FCSTD DOCUMENT  (FreeCAD 0.18R16131 (Git))
Label: plate_cutouts
License: All rights reserved
LicenseURL: http://en.wikipedia.org/wiki/All_rights_reserved
objects: Sketcher::SketchObject×6, Spreadsheet::Sheet×1
note: 6 computed .brp shape members not serialized (recipe doc carries the construction recipe); baked Part::Feature solids carry a one-line shape summary decoded from their .brp

FEATURE [Sketcher::SketchObject] Sketch  label="alps"
  expr: Constraints[10] = dimensions.alps_h + dimensions.oversize
  expr: Constraints[9] = dimensions.alps_w + dimensions.oversize
  sketch-geometry (4):
    g0: LineSegment StartX=-7.8 StartY=-6.4 StartZ=0 EndX=7.8 EndY=-6.4 EndZ=0
    g1: LineSegment StartX=7.8 StartY=-6.4 StartZ=0 EndX=7.8 EndY=6.4 EndZ=0
    g2: LineSegment StartX=7.8 StartY=6.4 StartZ=0 EndX=-7.8 EndY=6.4 EndZ=0
    g3: LineSegment StartX=-7.8 StartY=6.4 StartZ=0 EndX=-7.8 EndY=-6.4 EndZ=0
  constraints (11):
    c: Coincident(g0,g1)
    c: Coincident(g1,g2)
    c: Coincident(g2,g3)
    c: Coincident(g3,g0)
    c: Horizontal(g0)
    c: Horizontal(g2)
    c: Vertical(g1)
    c: Vertical(g3)
    c: Symmetric(g1,g0,g-1)
    c: Distance(g2) = 15.6
    c: Distance(g1) = 12.8
FEATURE [Sketcher::SketchObject] Sketch001  label="mx"
  MapMode = 5
  expr: Constraints[10] = dimensions.mx_h + dimensions.oversize
  expr: Constraints[9] = dimensions.mx_w + dimensions.oversize
  sketch-geometry (4):
    g0: LineSegment StartX=-7 StartY=-7 StartZ=0 EndX=7 EndY=-7 EndZ=0
    g1: LineSegment StartX=7 StartY=-7 StartZ=0 EndX=7 EndY=7 EndZ=0
    g2: LineSegment StartX=7 StartY=7 StartZ=0 EndX=-7 EndY=7 EndZ=0
    g3: LineSegment StartX=-7 StartY=7 StartZ=0 EndX=-7 EndY=-7 EndZ=0
  constraints (11):
    c: Coincident(g0,g1)
    c: Coincident(g1,g2)
    c: Coincident(g2,g3)
    c: Coincident(g3,g0)
    c: Horizontal(g0)
    c: Horizontal(g2)
    c: Vertical(g1)
    c: Vertical(g3)
    c: Symmetric(g1,g0,g-1)
    c: Distance(g2) = 14
    c: Distance(g1) = 14
FEATURE [Spreadsheet::Sheet] Spreadsheet  label="dimensions"
  cells = A2=mx height; B2(mx_h)=14; A3=mx width; B3(mx_w)=14; A5=alps height; B5(alps_h)=12.8; A6=alps width; B6(alps_w)=15.6; C6=nominal + 0.10; A8=corner radius; B8(in_rad)=0.5; A9=over/under size; B9(oversize)=0; A10=corner relief angle; B10(corner_angle)=45; A12=alps stab CU height; B12(alps_stab_cu_height)=5; A13=alps stab CU width; B13(alps_stab_cu_width)=2.5; A14=alps stab height pos; B14(alps_stab_pos_height)=9.1; A15=alps stab width pos; B15(alps_stab_pos_width)==31 / 2; A17=mx stab pos height; B17(mx_stab_pos_h)=6.77; A18=mx stab pos width; B18(mx_stab_pos_w)=15.33; C18=nominal + 0.05; A19=mx stab main height; B19(mx_stab_main_h)=12.4; C19=nominal + 0.10; A20=mx stab main width; B20(mx_stab_main_w)=6.85; C20=nominal + 0.10; A21=mx stab vert height; B21(mx_stab_vert_h)=13.5; A22=mx stab vert width; B22(mx_stab_vert_w)=3.3; A23=mx stab hor height; B23(mx_stab_hor_h)=2.8; A24=mx stab hor width; B24(mx_stab_hor_w)=7.65; C24=nominal + 0.10; A25=mx stab hor pos; B25(mx_stab_hor_pos)=6.27
FEATURE [Sketcher::SketchObject] Sketch002  label="mx_rounded"
  ExternalGeometry = -> [Sketch001]
  expr: Constraints[5] = dimensions.in_rad
  expr: Constraints[4] = dimensions.corner_angle
  sketch-geometry (12):
    g0: LineSegment [constr] StartX=-7 StartY=7 StartZ=0 EndX=-6.64645 EndY=6.64645 EndZ=0
    g1: LineSegment [constr] StartX=7 StartY=7 StartZ=0 EndX=6.64645 EndY=6.64645 EndZ=0
    g2: LineSegment [constr] StartX=7 StartY=-7 StartZ=0 EndX=6.64645 EndY=-6.64645 EndZ=0
    g3: LineSegment [constr] StartX=-7 StartY=-7 StartZ=0 EndX=-6.64645 EndY=-6.64645 EndZ=0
    g4: ArcOfCircle CenterX=-6.64645 CenterY=6.64645 CenterZ=0 NormalX=0 NormalY=0 NormalZ=1 AngleXU=0 Radius=0.5 StartAngle=0.785398 EndAngle=3.92699
    g5: ArcOfCircle CenterX=6.64645 CenterY=6.64645 CenterZ=0 NormalX=0 NormalY=0 NormalZ=1 AngleXU=0 Radius=0.5 StartAngle=5.49779 EndAngle=8.63938
    g6: ArcOfCircle CenterX=6.64645 CenterY=-6.64645 CenterZ=0 NormalX=0 NormalY=0 NormalZ=1 AngleXU=0 Radius=0.5 StartAngle=3.92699 EndAngle=7.06858
    g7: ArcOfCircle CenterX=-6.64645 CenterY=-6.64645 CenterZ=0 NormalX=0 NormalY=0 NormalZ=1 AngleXU=0 Radius=0.5 StartAngle=2.35619 EndAngle=5.49779
    g8: LineSegment StartX=-6.29289 StartY=7 StartZ=0 EndX=6.29289 EndY=7 EndZ=0
    g9: LineSegment StartX=-7 StartY=-6.29289 StartZ=0 EndX=-7 EndY=6.29289 EndZ=0
    g10: LineSegment StartX=7 StartY=6.29289 StartZ=0 EndX=7 EndY=-6.29289 EndZ=0
    g11: LineSegment StartX=6.29289 StartY=-7 StartZ=0 EndX=-6.29289 EndY=-7 EndZ=0
  constraints (33):
    c: Coincident(g0,g-4)
    c: Coincident(g1,g-6)
    c: Coincident(g2,g-6)
    c: Coincident(g3,g-5)
    c: Angle(g-4,g0) = 0.785398
    c: Distance(g0) = 0.5
    c: Symmetric(g1,g0,g-2)
    c: Symmetric(g0,g3,g-1)
    c: Symmetric(g3,g2,g-2)
    c: PointOnObject(g4,g-3)
    c: PointOnObject(g4,g-4)
    c: PointOnObject(g0,g4)
    c: Coincident(g4,g0)
    c: PointOnObject(g5,g-3)
    c: PointOnObject(g5,g-6)
    c: PointOnObject(g1,g5)
    c: Coincident(g5,g1)
    c: PointOnObject(g6,g-6)
    c: PointOnObject(g6,g-5)
    c: PointOnObject(g2,g6)
    c: Coincident(g6,g2)
    c: PointOnObject(g7,g-4)
    c: PointOnObject(g7,g-5)
    c: PointOnObject(g3,g7)
    c: Coincident(g7,g3)
    c: Coincident(g8,g4)
    c: Coincident(g9,g7)
    c: Coincident(g10,g5)
    c: Coincident(g11,g6)
    c: Coincident(g8,g5)
    c: Coincident(g10,g6)
    c: Coincident(g11,g7)
    c: Coincident(g9,g4)
FEATURE [Sketcher::SketchObject] Sketch003  label="alps_rounded"
  ExternalGeometry = -> [Sketch]
  MapMode = 2
  Support = -> [Sketch002]
  expr: Constraints[8] = dimensions.corner_angle
  expr: Constraints[3] = dimensions.in_rad
  sketch-geometry (12):
    g0: LineSegment [constr] StartX=-7.8 StartY=6.4 StartZ=0 EndX=-7.44645 EndY=6.04645 EndZ=0
    g1: LineSegment [constr] StartX=7.8 StartY=6.4 StartZ=0 EndX=7.44645 EndY=6.04645 EndZ=0
    g2: LineSegment [constr] StartX=7.8 StartY=-6.4 StartZ=0 EndX=7.44645 EndY=-6.04645 EndZ=0
    g3: LineSegment [constr] StartX=-7.8 StartY=-6.4 StartZ=0 EndX=-7.44645 EndY=-6.04645 EndZ=0
    g4: ArcOfCircle CenterX=-7.44645 CenterY=6.04645 CenterZ=0 NormalX=0 NormalY=0 NormalZ=1 AngleXU=0 Radius=0.5 StartAngle=0.785398 EndAngle=3.92699
    g5: ArcOfCircle CenterX=7.44645 CenterY=6.04645 CenterZ=0 NormalX=0 NormalY=0 NormalZ=1 AngleXU=0 Radius=0.5 StartAngle=5.49779 EndAngle=8.63938
    g6: ArcOfCircle CenterX=7.44645 CenterY=-6.04645 CenterZ=0 NormalX=0 NormalY=0 NormalZ=1 AngleXU=0 Radius=0.5 StartAngle=3.92699 EndAngle=7.06858
    g7: ArcOfCircle CenterX=-7.44645 CenterY=-6.04645 CenterZ=0 NormalX=0 NormalY=0 NormalZ=1 AngleXU=0 Radius=0.5 StartAngle=2.35619 EndAngle=5.49779
    g8: LineSegment StartX=-7.8 StartY=-5.69289 StartZ=0 EndX=-7.8 EndY=5.69289 EndZ=0
    g9: LineSegment StartX=-7.09289 StartY=6.4 StartZ=0 EndX=7.09289 EndY=6.4 EndZ=0
    g10: LineSegment StartX=7.8 StartY=5.69289 StartZ=0 EndX=7.8 EndY=-5.69289 EndZ=0
    g11: LineSegment StartX=7.09289 StartY=-6.4 StartZ=0 EndX=-7.09289 EndY=-6.4 EndZ=0
  constraints (33):
    c: Coincident(g1,g-6)
    c: Coincident(g2,g-6)
    c: Coincident(g3,g-5)
    c: Distance(g0) = 0.5
    c: Coincident(g0,g-4)
    c: Symmetric(g0,g1,g-2)
    c: Symmetric(g0,g3,g-1)
    c: Symmetric(g3,g2,g-2)
    c: Angle(g-4,g0) = 0.785398
    c: PointOnObject(g4,g-3)
    c: PointOnObject(g4,g-4)
    c: PointOnObject(g0,g4)
    c: Coincident(g4,g0)
    c: PointOnObject(g5,g-3)
    c: PointOnObject(g5,g-6)
    c: PointOnObject(g1,g5)
    c: Coincident(g5,g1)
    c: PointOnObject(g6,g-6)
    c: PointOnObject(g6,g-5)
    c: PointOnObject(g2,g6)
    c: Coincident(g6,g2)
    c: PointOnObject(g7,g-4)
    c: PointOnObject(g7,g-5)
    c: PointOnObject(g3,g7)
    c: Coincident(g7,g3)
    c: Coincident(g8,g7)
    c: Coincident(g9,g4)
    c: Coincident(g10,g5)
    c: Coincident(g11,g6)
    c: Coincident(g11,g7)
    c: Coincident(g8,g4)
    c: Coincident(g9,g5)
    c: Coincident(g10,g6)
FEATURE [Sketcher::SketchObject] Sketch004  label="mx_2u_stab"
  ExternalGeometry = -> [Sketch001]
  MapMode = 2
  Support = -> [Sketch003]
  expr: Constraints[36] = dimensions.mx_stab_pos_w
  expr: Constraints[34] = dimensions.mx_stab_hor_w + dimensions.oversize
  expr: Constraints[35] = dimensions.mx_stab_pos_h
  expr: Constraints[85] = dimensions.mx_stab_hor_pos
  expr: Constraints[33] = dimensions.mx_stab_vert_h + dimensions.oversize
  expr: Constraints[31] = dimensions.mx_stab_main_h + dimensions.oversize
  expr: Constraints[30] = dimensions.mx_stab_vert_w + dimensions.oversize
  expr: Constraints[32] = dimensions.mx_stab_hor_h + dimensions.oversize
  expr: Constraints[29] = dimensions.mx_stab_main_w + dimensions.oversize
  sketch-geometry (49):
    g0: LineSegment [constr] StartX=-8.48 StartY=5.63 StartZ=0 EndX=-8.48 EndY=-6.77 EndZ=0
    g1: LineSegment [constr] StartX=-8.48 StartY=-6.77 StartZ=0 EndX=-15.33 EndY=-6.77 EndZ=0
    g2: LineSegment [constr] StartX=-15.33 StartY=-6.77 StartZ=0 EndX=-15.33 EndY=5.63 EndZ=0
    g3: LineSegment [constr] StartX=-16.13 StartY=2.3 StartZ=0 EndX=-8.48 EndY=2.3 EndZ=0
    g4: LineSegment [constr] StartX=-8.48 StartY=2.3 StartZ=0 EndX=-8.48 EndY=-0.5 EndZ=0
    g5: LineSegment [constr] StartX=-8.48 StartY=-0.5 StartZ=0 EndX=-16.13 EndY=-0.5 EndZ=0
    g6: LineSegment [constr] StartX=-16.13 StartY=-0.5 StartZ=0 EndX=-16.13 EndY=2.3 EndZ=0
    g7: LineSegment [constr] StartX=-13.555 StartY=5.63 StartZ=0 EndX=-10.255 EndY=5.63 EndZ=0
    g8: LineSegment [constr] StartX=-10.255 StartY=5.63 StartZ=0 EndX=-10.255 EndY=-7.87 EndZ=0
    g9: LineSegment [constr] StartX=-10.255 StartY=-7.87 StartZ=0 EndX=-13.555 EndY=-7.87 EndZ=0
    g10: LineSegment [constr] StartX=-13.555 StartY=-7.87 StartZ=0 EndX=-13.555 EndY=5.63 EndZ=0
    g11: LineSegment [constr] StartX=-15.33 StartY=5.63 StartZ=0 EndX=-13.555 EndY=5.63 EndZ=0
    g12: LineSegment [constr] StartX=-10.255 StartY=5.63 StartZ=0 EndX=-8.48 EndY=5.63 EndZ=0
    g13: LineSegment StartX=-8.48 StartY=5.63 StartZ=0 EndX=-15.33 EndY=5.63 EndZ=0
    g14: LineSegment StartX=-15.33 StartY=5.63 StartZ=0 EndX=-15.33 EndY=2.3 EndZ=0
    g15: LineSegment StartX=-15.33 StartY=2.3 StartZ=0 EndX=-16.13 EndY=2.3 EndZ=0
    g16: LineSegment StartX=-16.13 StartY=2.3 StartZ=0 EndX=-16.13 EndY=-0.5 EndZ=0
    g17: LineSegment StartX=-16.13 StartY=-0.5 StartZ=0 EndX=-15.33 EndY=-0.5 EndZ=0
    g18: LineSegment StartX=-15.33 StartY=-0.5 StartZ=0 EndX=-15.33 EndY=-6.77 EndZ=0
    g19: LineSegment StartX=-15.33 StartY=-6.77 StartZ=0 EndX=-13.555 EndY=-6.77 EndZ=0
    g20: LineSegment StartX=-13.555 StartY=-6.77 StartZ=0 EndX=-13.555 EndY=-7.87 EndZ=0
    g21: LineSegment StartX=-13.555 StartY=-7.87 StartZ=0 EndX=-10.255 EndY=-7.87 EndZ=0
    g22: LineSegment StartX=-10.255 StartY=-7.87 StartZ=0 EndX=-10.255 EndY=-6.77 EndZ=0
    g23: LineSegment StartX=-10.255 StartY=-6.77 StartZ=0 EndX=-8.48 EndY=-6.77 EndZ=0
    g24: LineSegment StartX=8.48 StartY=5.63 StartZ=0 EndX=15.33 EndY=5.63 EndZ=0
    g25: LineSegment StartX=15.33 StartY=5.63 StartZ=0 EndX=15.33 EndY=2.3 EndZ=0
    g26: LineSegment StartX=15.33 StartY=2.3 StartZ=0 EndX=16.13 EndY=2.3 EndZ=0
    g27: LineSegment StartX=16.13 StartY=2.3 StartZ=0 EndX=16.13 EndY=-0.5 EndZ=0
    g28: LineSegment StartX=16.13 StartY=-0.5 StartZ=0 EndX=15.33 EndY=-0.5 EndZ=0
    g29: LineSegment StartX=15.33 StartY=-0.5 StartZ=0 EndX=15.33 EndY=-6.77 EndZ=0
    g30: LineSegment StartX=15.33 StartY=-6.77 StartZ=0 EndX=13.555 EndY=-6.77 EndZ=0
    g31: LineSegment StartX=13.555 StartY=-7.87 StartZ=0 EndX=10.255 EndY=-7.87 EndZ=0
    g32: LineSegment StartX=13.555 StartY=-6.77 StartZ=0 EndX=13.555 EndY=-7.87 EndZ=0
    g33: LineSegment StartX=10.255 StartY=-7.87 StartZ=0 EndX=10.255 EndY=-6.77 EndZ=0
    g34: LineSegment StartX=10.255 StartY=-6.77 StartZ=0 EndX=8.48 EndY=-6.77 EndZ=0
    g35: LineSegment StartX=-7 StartY=3.7 StartZ=0 EndX=-7 EndY=7 EndZ=0
    g36: LineSegment StartX=-7 StartY=7 StartZ=0 EndX=7 EndY=7 EndZ=0
    g37: LineSegment StartX=7 StartY=7 StartZ=0 EndX=7 EndY=3.7 EndZ=0
    g38: LineSegment StartX=7 StartY=3.7 StartZ=0 EndX=8.48 EndY=3.7 EndZ=0
    g39: LineSegment StartX=8.48 StartY=3.7 StartZ=0 EndX=8.48 EndY=5.63 EndZ=0
    g40: LineSegment StartX=-7 StartY=-3.7 StartZ=0 EndX=-7 EndY=-7 EndZ=0
    g41: LineSegment StartX=-7 StartY=-7 StartZ=0 EndX=7 EndY=-7 EndZ=0
    g42: LineSegment StartX=7 StartY=-7 StartZ=0 EndX=7 EndY=-3.7 EndZ=0
    g43: LineSegment StartX=7 StartY=-3.7 StartZ=0 EndX=8.48 EndY=-3.7 EndZ=0
    g44: LineSegment StartX=8.48 StartY=-3.7 StartZ=0 EndX=8.48 EndY=-6.77 EndZ=0
    g45: LineSegment StartX=-7 StartY=-3.7 StartZ=0 EndX=-8.48 EndY=-3.7 EndZ=0
    g46: LineSegment StartX=-8.48 StartY=-3.7 StartZ=0 EndX=-8.48 EndY=-6.77 EndZ=0
    g47: LineSegment StartX=-8.48 StartY=5.63 StartZ=0 EndX=-8.48 EndY=3.7 EndZ=0
    g48: LineSegment StartX=-8.48 StartY=3.7 StartZ=0 EndX=-7 EndY=3.7 EndZ=0
  constraints (122):
    c: Coincident(g0,g1)
    c: Coincident(g1,g2)
    c: Horizontal(g1)
    c: Vertical(g0)
    c: Vertical(g2)
    c: Coincident(g3,g4)
    c: Coincident(g4,g5)
    c: Coincident(g5,g6)
    c: Coincident(g6,g3)
    c: Horizontal(g3)
    c: Horizontal(g5)
    c: Vertical(g4)
    c: Vertical(g6)
    c: PointOnObject(g4,g0)
    c: Coincident(g7,g8)
    c: Coincident(g8,g9)
    c: Coincident(g9,g10)
    c: Coincident(g10,g7)
    c: Horizontal(g7)
    c: Horizontal(g9)
    c: Vertical(g8)
    c: Vertical(g10)
    c: Coincident(g11,g2)
    c: Coincident(g11,g7)
    c: Horizontal(g11)
    c: Coincident(g12,g7)
    c: Coincident(g12,g0)
    c: Horizontal(g12)
    c: Equal(g12,g11)
    c: DistanceX(g2,g0) = 6.85
    c: DistanceX(g7,g7) = 3.3
    c: DistanceY(g1,g2) = 12.4
    c: DistanceY(g5,g3) = 2.8
    c: DistanceY(g9,g7) = 13.5
    c: DistanceX(g3,g3) = 7.65
    c: DistanceY(g0,g-1) = 6.77
    c: DistanceX(g1,g-1) = 15.33
    c: Coincident(g0,g13)
    c: Coincident(g13,g14)
    c: Coincident(g14,g15)
    c: Coincident(g15,g16)
    c: Coincident(g16,g17)
    c: Coincident(g17,g18)
    c: Coincident(g18,g19)
    c: Coincident(g19,g20)
    c: Coincident(g21,g22)
    c: Coincident(g22,g23)
    c: Coincident(g13,g2)
    c: Coincident(g15,g3)
    c: Coincident(g16,g5)
    c: Coincident(g18,g1)
    c: Coincident(g20,g9)
    c: Coincident(g21,g20)
    c: Coincident(g21,g8)
    c: Coincident(g23,g0)
    c: Vertical(g14)
    c: Vertical(g18)
    c: Vertical(g20)
    c: Vertical(g22)
    c: Horizontal(g15)
    c: Horizontal(g17)
    c: Horizontal(g19)
    c: Horizontal(g23)
    c: Coincident(g24,g25)
    c: Coincident(g25,g26)
    c: Coincident(g26,g27)
    c: Coincident(g27,g28)
    c: Coincident(g28,g29)
    c: Coincident(g29,g30)
    c: Coincident(g30,g32)
    c: Coincident(g31,g33)
    c: Coincident(g33,g34)
    c: Coincident(g31,g32)
    c: Symmetric(g13,g24,g-2)
    c: Symmetric(g13,g24,g-2)
    c: Symmetric(g14,g25,g-2)
    c: Symmetric(g26,g15,g-2)
    c: Symmetric(g16,g27,g-2)
    c: Symmetric(g28,g17,g-2)
    c: Symmetric(g18,g29,g-2)
    c: Symmetric(g30,g19,g-2)
    c: Symmetric(g20,g31,g-2)
    c: Symmetric(g31,g21,g-2)
    c: Symmetric(g22,g33,g-2)
    c: Symmetric(g34,g23,g-2)
    c: DistanceY(g23,g4) = 6.27
    c: PointOnObject(g35,g-3)
    c: Coincident(g35,g36)
    c: Coincident(g36,g37)
    c: PointOnObject(g37,g-4)
    c: Coincident(g37,g38)
    c: Horizontal(g38)
    c: Coincident(g38,g39)
    c: Coincident(g39,g24)
    c: Coincident(g35,g-5)
    c: Coincident(g36,g-5)
    c: Equal(g35,g37)
    c: PointOnObject(g40,g-3)
    c: Coincident(g40,g41)
    c: Coincident(g41,g42)
    c: PointOnObject(g42,g-4)
    c: Coincident(g42,g43)
    c: Horizontal(g43)
    c: Coincident(g43,g44)
    c: Coincident(g44,g34)
    c: Coincident(g41,g-6)
    c: Coincident(g-6,g40)
    c: Coincident(g40,g45)
    c: PointOnObject(g45,g0)
    c: Horizontal(g45)
    c: Coincident(g45,g46)
    c: Coincident(g46,g23)
    c: Equal(g46,g44)
    c: Coincident(g13,g47)
    c: Coincident(g47,g48)
    c: Coincident(g48,g35)
    c: Vertical(g47)
    c: Horizontal(g48)
    c: Equal(g35,g40)
    c: Equal(g35,g21)
    c: Vertical(g39)
    c: Vertical(g44)
FEATURE [Sketcher::SketchObject] Sketch005  label="alps_2u_stab"
  expr: Constraints[22] = dimensions.alps_stab_pos_width
  expr: Constraints[21] = dimensions.alps_stab_pos_height
  expr: Constraints[20] = dimensions.alps_stab_cu_height + dimensions.oversize
  expr: Constraints[19] = dimensions.alps_stab_cu_width + dimensions.oversize
  sketch-geometry (8):
    g0: LineSegment StartX=13 StartY=-4.1 StartZ=0 EndX=15.5 EndY=-4.1 EndZ=0
    g1: LineSegment StartX=15.5 StartY=-4.1 StartZ=0 EndX=15.5 EndY=-9.1 EndZ=0
    g2: LineSegment StartX=15.5 StartY=-9.1 StartZ=0 EndX=13 EndY=-9.1 EndZ=0
    g3: LineSegment StartX=13 StartY=-9.1 StartZ=0 EndX=13 EndY=-4.1 EndZ=0
    g4: LineSegment StartX=-13 StartY=-4.1 StartZ=0 EndX=-15.5 EndY=-4.1 EndZ=0
    g5: LineSegment StartX=-15.5 StartY=-4.1 StartZ=0 EndX=-15.5 EndY=-9.1 EndZ=0
    g6: LineSegment StartX=-15.5 StartY=-9.1 StartZ=0 EndX=-13 EndY=-9.1 EndZ=0
    g7: LineSegment StartX=-13 StartY=-9.1 StartZ=0 EndX=-13 EndY=-4.1 EndZ=0
  constraints (23):
    c: Coincident(g0,g1)
    c: Coincident(g1,g2)
    c: Coincident(g2,g3)
    c: Coincident(g3,g0)
    c: Horizontal(g0)
    c: Horizontal(g2)
    c: Vertical(g1)
    c: Vertical(g3)
    c: Coincident(g4,g5)
    c: Coincident(g5,g6)
    c: Coincident(g6,g7)
    c: Coincident(g7,g4)
    c: Horizontal(g4)
    c: Horizontal(g6)
    c: Vertical(g5)
    c: Vertical(g7)
    c: Symmetric(g0,g4,g-2)
    c: Equal(g0,g4)
    c: Equal(g7,g3)
    c: Distance(g4) = 2.5
    c: Distance(g5) = 5
    c: DistanceY(g6,g-1) = 9.1
    c: DistanceX(g4,g-1) = 15.5
